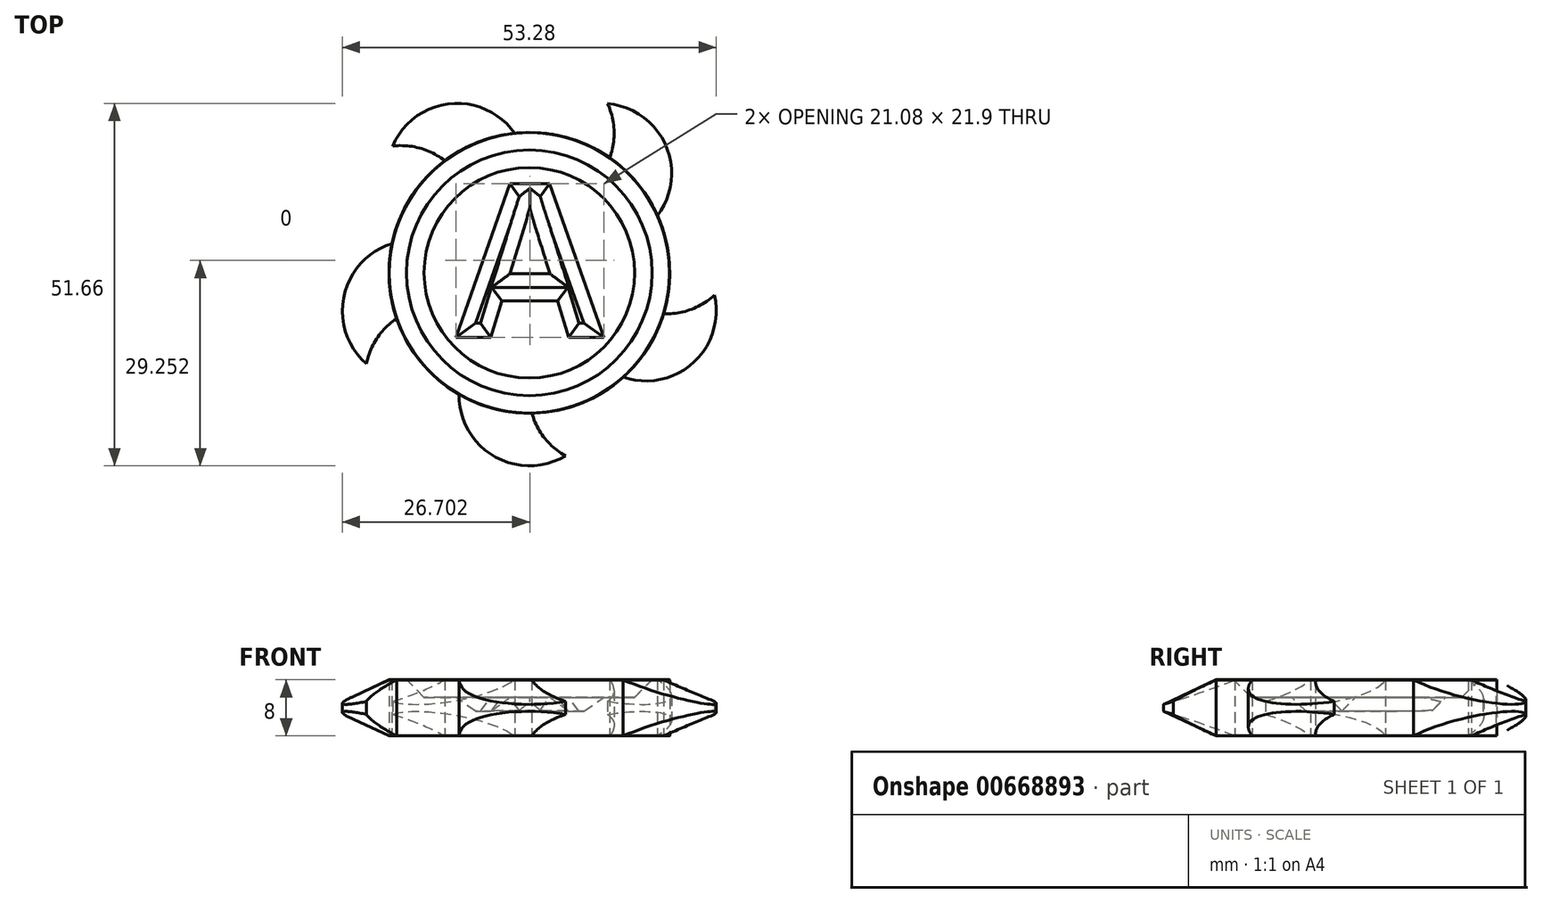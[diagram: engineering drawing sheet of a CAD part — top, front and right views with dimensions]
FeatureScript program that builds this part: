
annotation { "Feature Type Name" : "Feature", "Feature Type Description" : "" }
export const myFeature = defineFeature(function(context is Context, id is Id, definition is map)
    precondition{}
    {
        {
            var Q0;
            Q0=qCreatedBy(makeId("Top.planeOp"),FACE);
            var sketch = newSketch(context, id + "F0", { "sketchPlane" : qUnion([Q0])});
            skCircle(sketch, "E0", {"center": v(0, 0) * mm, "radius": 20 * mm});
            skSolve(sketch);
        }
        {
            var Q0;
            Q0=makeQuery(id+"F0.imprint","IMPRINT",FACE,{"disambiguationData":[TD([[makeQuery(id+"F0.imprint","IMPRINT",EDGE,{"derivedFrom":sQuery(id+"F0.wireOp",EDGE,"E0")}),1.0]])]});
            extrude(context, id + "F1", {"entities" : qUnion([Q0]), "endBound" : BoundingType.SYMMETRIC, "depth" : 8 * mm, "offsetDistance" : 25 * mm});
        }
        {
            var Q0;
            Q0=makeQuery(id+"F1.opExtrude","CAP_FACE",FACE,{"disambiguationData":[OSD([sQuery(id+"F0.wireOp",EDGE,"E0")])],"isStart":false});
            var sketch = newSketch(context, id + "F2", { "sketchPlane" : qUnion([Q0])});
            skCircle(sketch, "E1", {"center": v(0, 0) * mm, "radius": 17.5 * mm});
            skSolve(sketch);
        }
        {
            var Q0;
            Q0=makeQuery(id+"F2.imprint","IMPRINT",FACE,{"disambiguationData":[TD([[makeQuery(id+"F2.imprint","IMPRINT",EDGE,{"derivedFrom":sQuery(id+"F2.wireOp",EDGE,"E1")}),1.0]])]});
            extrude(context, id + "F3", {"entities" : qUnion([Q0]), "operationType" : NewBodyOperationType.REMOVE, "oppositeDirection" : true, "depth" : 2.5 * mm, "offsetDistance" : 25 * mm, "hasDraft" : true, "draftAngle" : 45 * degree, "draftPullDirection" : true});
        }
        {
            var Q0;
            Q0=qCreatedBy(makeId("Top.planeOp"),FACE);
            var sketch = newSketch(context, id + "F4", { "sketchPlane" : qUnion([Q0])});
            skCircle(sketch, "E2", {"center": v(0, 0) * mm, "radius": 17.5 * mm});
            skLineSegment(sketch, "E3", {"start": v(0, 0) * mm, "end": v(0, -17.5) * mm});
            skCircle(sketch, "E4", {"center": v(0, -17.5) * mm, "radius": 10 * mm});
            skCircle(sketch, "E5", {"center": v(0, 0) * mm, "radius": 20 * mm});
            skCircle(sketch, "E6", {"center": v(10, -17.32) * mm, "radius": 10 * mm});
            skSolve(sketch);
        }
        {
            var Q0;
            {var subQ0=sQuery(id+"F4.wireOp",EDGE,"E5");var subQ1=sQuery(id+"F4.wireOp",EDGE,"E4");var subQ2=makeQuery(id+"F4.imprint","INTERSECT",VERTEX,{"disambiguationData":[OD(0.0)],"derivedFrom":[subQ1,subQ0]});Q0=makeQuery(id+"F4.imprint","IMPRINT",FACE,{"disambiguationData":[TD([[makeQuery(id+"F4.imprint","IMPRINT",EDGE,{"disambiguationData":[TD([[subQ2,-1.0]])],"derivedFrom":subQ1}),1.0]])]});}
            extrude(context, id + "F5", {"entities" : qUnion([Q0]), "operationType" : NewBodyOperationType.ADD, "endBound" : BoundingType.SYMMETRIC, "depth" : 8 * mm, "offsetDistance" : 25 * mm});
        }
        {
            var Q0;
            Q0=qCreatedBy(makeId("Front.planeOp"),FACE);
            var sketch = newSketch(context, id + "F6", { "sketchPlane" : qUnion([Q0])});
            skLineSegment(sketch, "E7", {"start": v(0, 5.93) * mm, "end": v(0, -6.64) * mm});
            skSolve(sketch);
        }
        {
            var Q0;
            Q0=makeQuery(id+"F1.opExtrude","SWEPT_BODY",BODY,{"disambiguationData":[OSD([sQuery(id+"F0.wireOp",EDGE,"E0")])]});
            var Q1;
            Q1=sQuery(id+"F6.wireOp",EDGE,"E7");
            circularPattern(context, id + "F7", {"entities" : qUnion([Q0]), "axis" : qUnion([Q1]), "angle" : 360 * degree, "instanceCount" : 5, "equalSpace" : true});
        }
        {
            var Q0;
            Q0=makeQuery(id+"F3.boolean.opBoolean","COPY",FACE,{"derivedFrom":makeQuery(id+"F3.opExtrude","CAP_FACE",FACE,{"disambiguationData":[OSD([sQuery(id+"F2.wireOp",EDGE,"E1")])],"isStart":false})});
            var sketch = newSketch(context, id + "F8", { "sketchPlane" : qUnion([Q0])});
            skText(sketch, "E8", { "text": "A", "fontName": "OpenSans-Bold.ttf"});
            const initialGuessF8  = {"E8": [-0.01048, -0.0092, 1, 0, 0.022]};
            skSetInitialGuess(sketch, initialGuessF8);
            skSolve(sketch);
        }
        {
            var Q0;
            Q0=makeQuery(id+"F8.imprint","IMPRINT",FACE,{"disambiguationData":[TD([[makeQuery(id+"F8.imprint","IMPRINT",EDGE,{"derivedFrom":sQuery(id+"F8.wireOp",EDGE,"E8.sketch_text.stroke-0")}),-1.0]])]});
            extrude(context, id + "F9", {"entities" : qUnion([Q0]), "operationType" : NewBodyOperationType.REMOVE, "oppositeDirection" : true, "depth" : 2 * mm, "offsetDistance" : 25 * mm, "hasDraft" : true, "draftAngle" : 45 * degree, "draftPullDirection" : true});
        }
        {
            var Q0;
            Q0=qCreatedBy(makeId("Right.planeOp"),FACE);
            var sketch = newSketch(context, id + "F10", { "sketchPlane" : qUnion([Q0])});
            skLineSegment(sketch, "E9", {"start": v(0, 0) * mm, "end": v(-34.73, 0) * mm});
            skLineSegment(sketch, "E10", {"start": v(-34.73, 0) * mm, "end": v(-34.73, 5.17) * mm});
            skLineSegment(sketch, "E11", {"start": v(-34.73, 5.17) * mm, "end": v(-17.49, 5.17) * mm});
            skLineSegment(sketch, "E12", {"start": v(-17.49, 5.17) * mm, "end": v(-28.57, 0) * mm});
            skLineSegment(sketch, "E13.MirrorCS", {"start": v(-17.49, -5.17) * mm, "end": v(-28.57, 0) * mm});
            skLineSegment(sketch, "E14.MirrorCS", {"start": v(-34.73, -5.17) * mm, "end": v(-17.49, -5.17) * mm});
            skLineSegment(sketch, "E15.MirrorCS", {"start": v(-34.73, 0) * mm, "end": v(-34.73, -5.17) * mm});
            skSolve(sketch);
        }
        {
            var Q0;
            {var subQ0=sQuery(id+"F10.wireOp",EDGE,"E10");Q0=makeQuery(id+"F10.imprint","IMPRINT",FACE,{"disambiguationData":[TD([[makeQuery(id+"F10.imprint","IMPRINT",EDGE,{"derivedFrom":subQ0}),-1.0]])]});}
            var Q1;
            {var subQ2=sQuery(id+"F10.wireOp",EDGE,"E13.MirrorCS");Q1=makeQuery(id+"F10.imprint","IMPRINT",FACE,{"disambiguationData":[TD([[makeQuery(id+"F10.imprint","IMPRINT",EDGE,{"derivedFrom":subQ2}),1.0]])]});}
            var Q2;
            Q2=sQuery(id+"F6.wireOp",EDGE,"E7");
            revolve(context, id + "F11", {"operationType" : NewBodyOperationType.REMOVE, "entities" : qUnion([Q0, Q1]), "axis" : qUnion([Q2]), "revolveType" : RevolveType.FULL, "oppositeDirection" : true});
        }
    });
